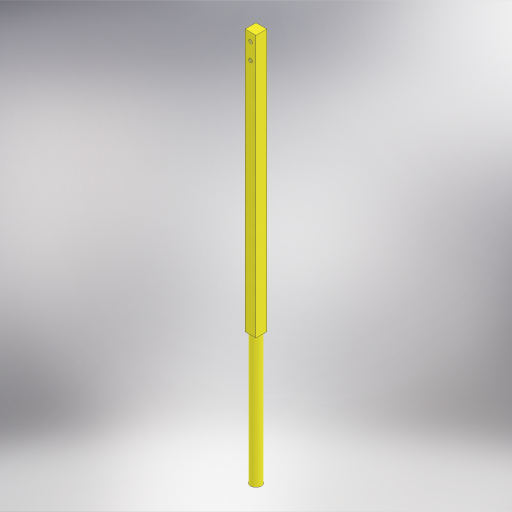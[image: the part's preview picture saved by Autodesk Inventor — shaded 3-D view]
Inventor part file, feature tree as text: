
AUTODESK INVENTOR PART (.ipt)
format: ipt  version: 2024 (Build 280153000, 153)  size: 348,672 bytes
history: native  units: in
note: dims shown in document units (in); Inventor stores cm internally (conversion verified against a paired STEP export)
features: extrude x2, hole x1
ambient origin geometry x8: Origin, YZ Plane, XZ Plane, XY Plane, X Axis, Y Axis, Z Axis, Center Point
bodies: Solid1 (feature_tree)
feature tree (3):
  extrude  "Extrusion1"  Depth=0.25in
  extrude  "Extrusion3"  Depth=0.25in
  hole  "Hole1"  [1 undecoded]
note: 1 required parameter value undecoded (feature->parameter linkage not recoverable at this tier; creation-order binding heuristic only, values carry confidence <= 0.55)
